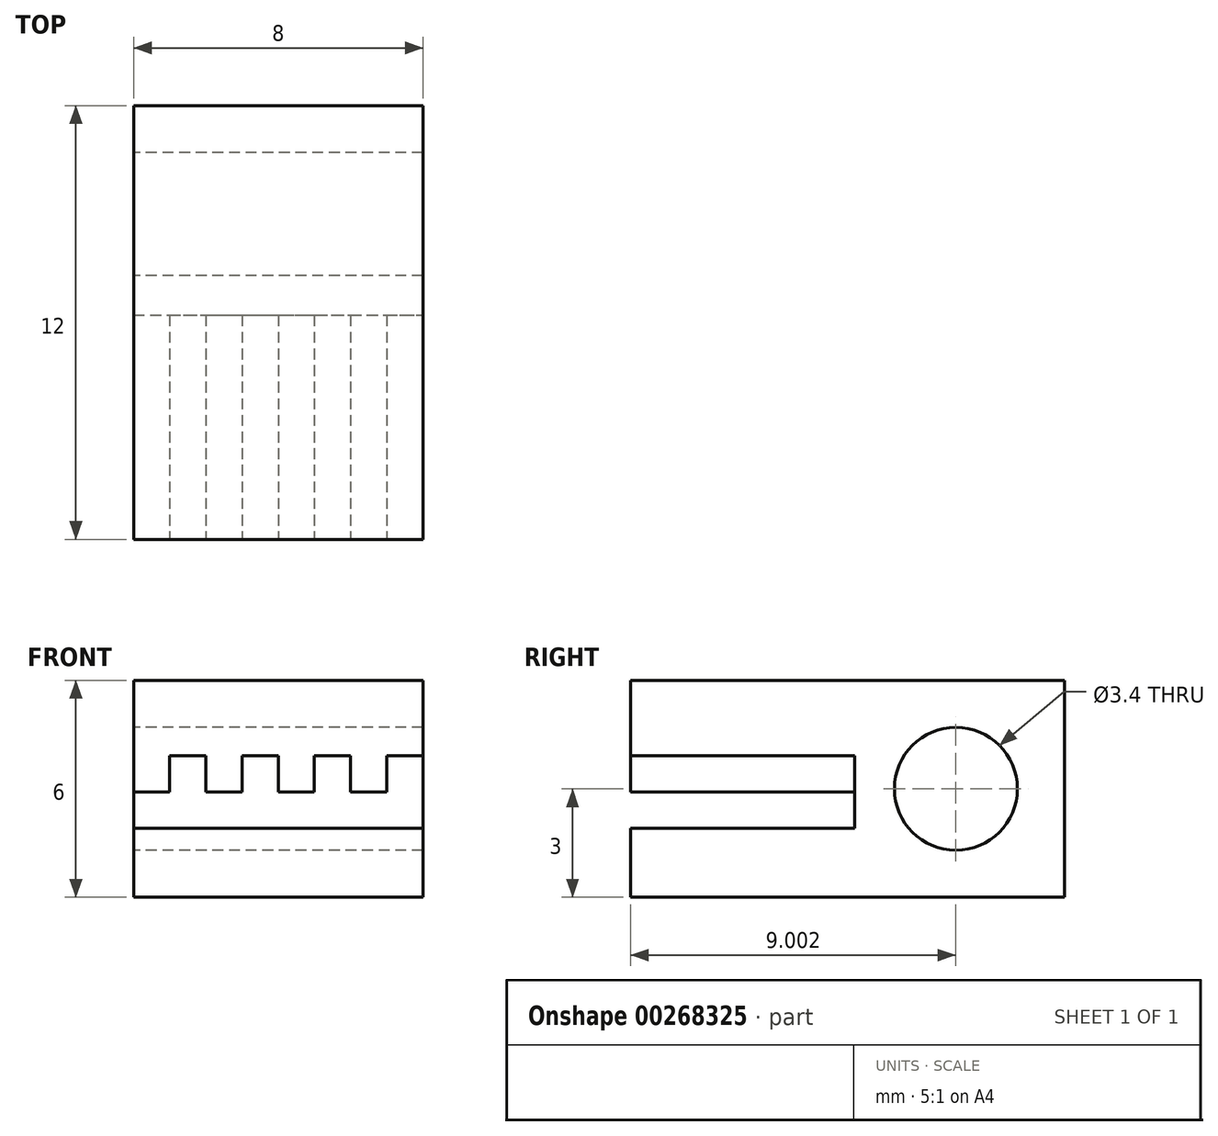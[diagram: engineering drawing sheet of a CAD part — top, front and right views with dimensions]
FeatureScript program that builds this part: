
annotation { "Feature Type Name" : "Feature", "Feature Type Description" : "" }
export const myFeature = defineFeature(function(context is Context, id is Id, definition is map)
    precondition{}
    {
        {
            var Q0;
            Q0=qCreatedBy(makeId("Top.planeOp"),FACE);
            var sketch = newSketch(context, id + "F0", { "sketchPlane" : qUnion([Q0])});
            skLineSegment(sketch, "E0.bottom", {"start": v(6.14, 7.11) * mm, "end": v(14.14, 7.11) * mm});
            skLineSegment(sketch, "E0.top", {"start": v(6.14, -4.89) * mm, "end": v(14.14, -4.89) * mm});
            skLineSegment(sketch, "E0.left", {"start": v(6.14, 7.11) * mm, "end": v(6.14, -4.89) * mm});
            skLineSegment(sketch, "E0.right", {"start": v(14.14, 7.11) * mm, "end": v(14.14, -4.89) * mm});
            skSolve(sketch);
        }
        {
            var Q0;
            Q0=qSketchRegion(id+"F0",true);
            extrude(context, id + "F1", {"entities" : qUnion([Q0]), "depth" : 6 * mm});
        }
        {
            var Q0;
            Q0=makeQuery(id+"F1.opExtrude","SWEPT_FACE",FACE,{"disambiguationData":[OSD([sQuery(id+"F0.wireOp",EDGE,"E0.top")])]});
            var sketch = newSketch(context, id + "F2", { "sketchPlane" : qUnion([Q0])});
            skLineSegment(sketch, "E1", {"start": v(6.14, 1.91) * mm, "end": v(14.14, 1.91) * mm});
            skLineSegment(sketch, "E2", {"start": v(6.14, 2.91) * mm, "end": v(7.14, 2.91) * mm});
            skLineSegment(sketch, "E3", {"start": v(7.14, 2.91) * mm, "end": v(7.14, 3.91) * mm});
            skLineSegment(sketch, "E4", {"start": v(7.14, 3.91) * mm, "end": v(8.14, 3.91) * mm});
            skLineSegment(sketch, "E5", {"start": v(8.14, 3.91) * mm, "end": v(8.14, 2.91) * mm});
            skLineSegment(sketch, "E6.1.0.0", {"start": v(10.14, 3.91) * mm, "end": v(10.14, 2.91) * mm});
            skLineSegment(sketch, "E6.1.0.1", {"start": v(9.14, 3.91) * mm, "end": v(10.14, 3.91) * mm});
            skLineSegment(sketch, "E6.1.0.2", {"start": v(9.14, 2.91) * mm, "end": v(9.14, 3.91) * mm});
            skLineSegment(sketch, "E6.1.0.3", {"start": v(8.14, 2.91) * mm, "end": v(9.14, 2.91) * mm});
            skLineSegment(sketch, "E6.2.0.0", {"start": v(12.14, 3.91) * mm, "end": v(12.14, 2.91) * mm});
            skLineSegment(sketch, "E6.2.0.1", {"start": v(11.14, 3.91) * mm, "end": v(12.14, 3.91) * mm});
            skLineSegment(sketch, "E6.2.0.2", {"start": v(11.14, 2.91) * mm, "end": v(11.14, 3.91) * mm});
            skLineSegment(sketch, "E6.2.0.3", {"start": v(10.14, 2.91) * mm, "end": v(11.14, 2.91) * mm});
            skLineSegment(sketch, "E6.3.0.0", {"start": v(14.14, 3.91) * mm, "end": v(14.14, 2.91) * mm});
            skLineSegment(sketch, "E6.3.0.1", {"start": v(13.14, 3.91) * mm, "end": v(14.14, 3.91) * mm});
            skLineSegment(sketch, "E6.3.0.2", {"start": v(13.14, 2.91) * mm, "end": v(13.14, 3.91) * mm});
            skLineSegment(sketch, "E6.3.0.3", {"start": v(12.14, 2.91) * mm, "end": v(13.14, 2.91) * mm});
            skLineSegment(sketch, "E6.direction1", {"start": v(6.14, 2.91) * mm, "end": v(8.14, 2.91) * mm, "construction": true});
            skSolve(sketch);
        }
        {
            var Q0;
            {var subQ1=sQuery(id+"F2.wireOp",EDGE,"E1");Q0=makeQuery(id+"F2.imprint","IMPRINT",FACE,{"disambiguationData":[TD([[makeQuery(id+"F2.imprint","IMPRINT",EDGE,{"derivedFrom":subQ1}),1.0]])]});}
            extrude(context, id + "F3", {"entities" : qUnion([Q0]), "operationType" : NewBodyOperationType.REMOVE, "oppositeDirection" : true, "depth" : 6.2 * mm});
        }
        {
            var Q0;
            Q0=makeQuery(id+"F1.opExtrude","SWEPT_FACE",FACE,{"disambiguationData":[OSD([sQuery(id+"F0.wireOp",EDGE,"E0.left")])]});
            var sketch = newSketch(context, id + "F4", { "sketchPlane" : qUnion([Q0])});
            skCircle(sketch, "E7", {"center": v(-4.11, 3) * mm, "radius": 1.7 * mm});
            skPoint(sketch, "E7.centerSnap0", {"position": v(-7.11, 3) * mm});
            skSolve(sketch);
        }
        {
            var Q0;
            Q0=qSketchRegion(id+"F4",true);
            extrude(context, id + "F5", {"entities" : qUnion([Q0]), "operationType" : NewBodyOperationType.REMOVE, "oppositeDirection" : true, "depth" : 25 * mm});
        }
    });
